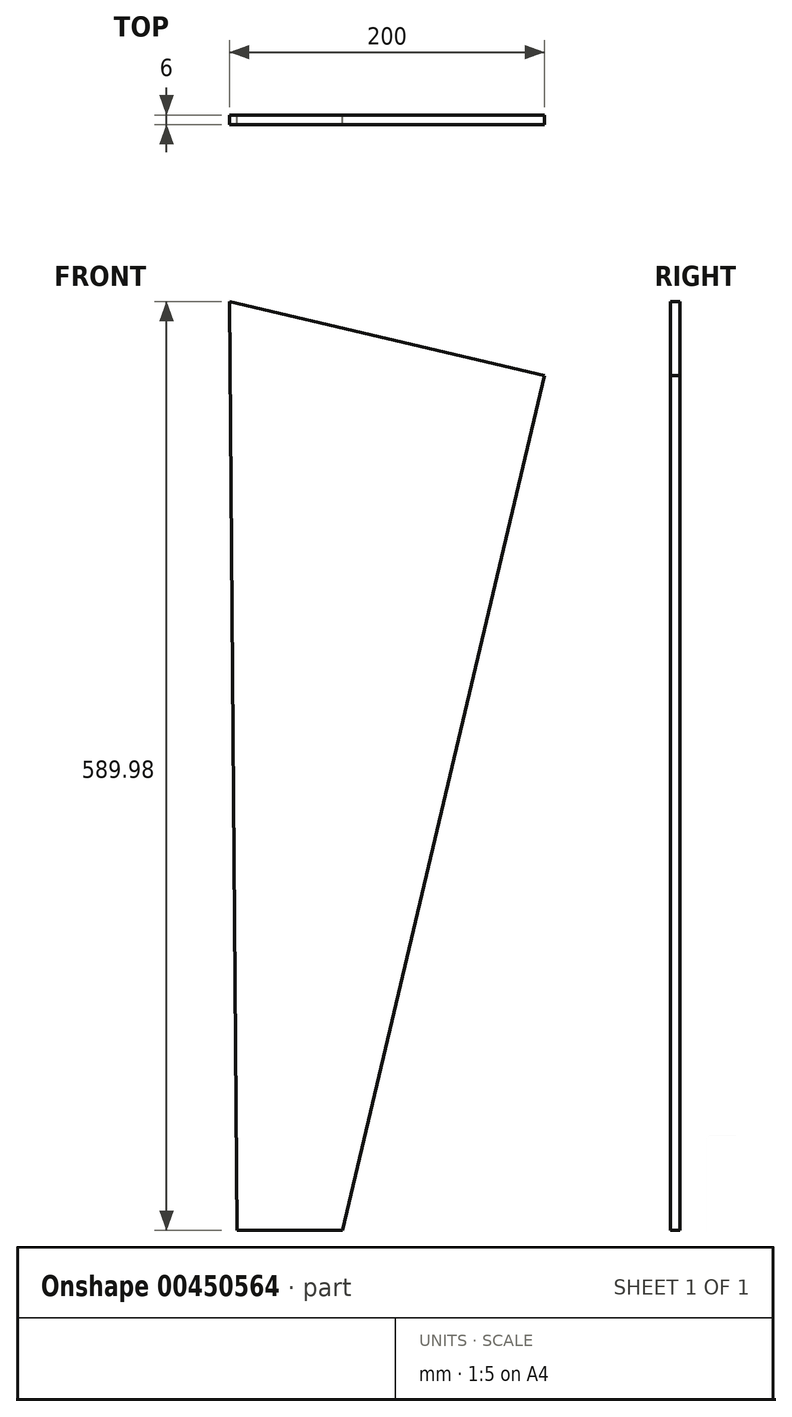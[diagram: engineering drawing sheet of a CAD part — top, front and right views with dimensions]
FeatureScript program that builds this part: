
annotation { "Feature Type Name" : "Feature", "Feature Type Description" : "" }
export const myFeature = defineFeature(function(context is Context, id is Id, definition is map)
    precondition{}
    {
        {
            var Q0;
            Q0=qCreatedBy(makeId("Front.planeOp"),FACE);
            var sketch = newSketch(context, id + "F0", { "sketchPlane" : qUnion([Q0])});
            skLineSegment(sketch, "E0", {"start": v(4.76, 0) * mm, "end": v(71.76, 0) * mm});
            skLineSegment(sketch, "E1", {"start": v(71.76, 0) * mm, "end": v(200, 543.06) * mm});
            skLineSegment(sketch, "E2", {"start": v(200, 543.06) * mm, "end": v(0, 589.98) * mm});
            skLineSegment(sketch, "E3", {"start": v(0, 589.98) * mm, "end": v(4.76, 0) * mm});
            skSolve(sketch);
        }
        {
            var Q0;
            Q0 = qSketchRegion(id + "F0", true);
            extrude(context, id + "F1", {"entities" : qUnion([Q0]), "depth" : 6 * mm});
        }
    });
